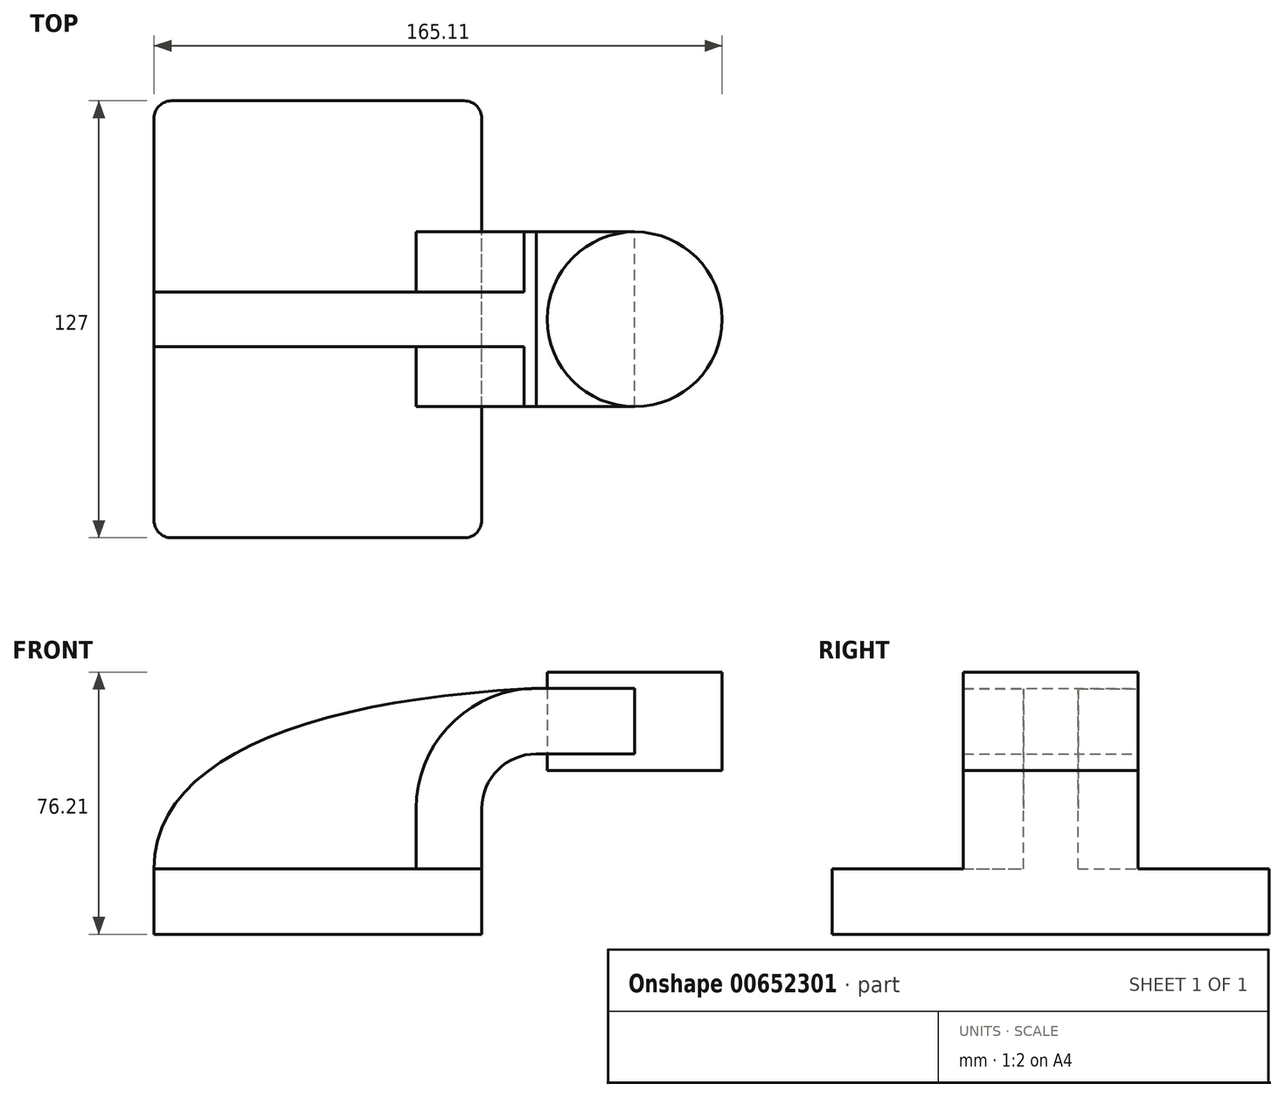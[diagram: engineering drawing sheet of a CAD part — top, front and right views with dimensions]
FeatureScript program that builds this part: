
annotation { "Feature Type Name" : "Feature", "Feature Type Description" : "" }
export const myFeature = defineFeature(function(context is Context, id is Id, definition is map)
    precondition{}
    {
        {
            var Q0;
            Q0=qCreatedBy(makeId("Front.planeOp"),FACE);
            var sketch = newSketch(context, id + "F0", { "sketchPlane" : qUnion([Q0])});
            skLineSegment(sketch, "E0.bottom", {"start": v(47.63, -9.52) * mm, "end": v(-47.62, -9.52) * mm});
            skLineSegment(sketch, "E0.top", {"start": v(47.62, 9.53) * mm, "end": v(-47.62, 9.53) * mm});
            skLineSegment(sketch, "E0.left", {"start": v(47.63, -9.52) * mm, "end": v(47.62, 9.53) * mm});
            skLineSegment(sketch, "E0.right", {"start": v(-47.62, -9.52) * mm, "end": v(-47.62, 9.53) * mm});
            skPoint(sketch, "E0.middle", {"position": v(0, 0) * mm});
            skLineSegment(sketch, "E1.bottom", {"start": v(66.67, 66.68) * mm, "end": v(117.47, 66.68) * mm});
            skLineSegment(sketch, "E1.top", {"start": v(66.67, 38.1) * mm, "end": v(117.47, 38.1) * mm});
            skLineSegment(sketch, "E1.left", {"start": v(66.67, 66.68) * mm, "end": v(66.67, 38.1) * mm});
            skLineSegment(sketch, "E1.right", {"start": v(117.47, 66.68) * mm, "end": v(117.47, 38.1) * mm});
            skPoint(sketch, "E1.middle", {"position": v(92.07, 52.39) * mm});
            skLineSegment(sketch, "E2", {"start": v(47.62, 9.53) * mm, "end": v(47.62, 27) * mm});
            skArc(sketch, "E3", {"start": v(47.62, 27) * mm, "mid": v(52.27, 38.23) * mm, "end": v(63.5, 42.88) * mm});
            skLineSegment(sketch, "E4", {"start": v(63.5, 42.88) * mm, "end": v(92.08, 42.88) * mm});
            skLineSegment(sketch, "E5.0", {"start": v(63.5, 61.93) * mm, "end": v(92.08, 61.93) * mm});
            skArc(sketch, "E5.1", {"start": v(28.58, 27) * mm, "mid": v(38.8, 51.7) * mm, "end": v(63.5, 61.93) * mm});
            skLineSegment(sketch, "E5.2", {"start": v(28.58, 9.53) * mm, "end": v(28.58, 27) * mm});
            skFitSpline(sketch, "E6", {"points": [v(-47.62, 9.53) * mm, v(63.5, 61.93) * mm], "startDerivative": vector(0.22, 99.5) * mm, "endDerivative": vector(190.5, 8.86) * mm});
            skLineSegment(sketch, "E7", {"start": v(92.07, 38.1) * mm, "end": v(92.07, 66.68) * mm});
            skSolve(sketch);
        }
        {
            var Q0;
            Q0=makeQuery(id+"F0.imprint","IMPRINT",FACE,{"disambiguationData":[TD([[makeQuery(id+"F0.imprint","IMPRINT",EDGE,{"derivedFrom":sQuery(id+"F0.wireOp",EDGE,"E0.bottom")}),-1.0]])]});
            extrude(context, id + "F1", {"entities" : qUnion([Q0]), "endBound" : BoundingType.SYMMETRIC, "depth" : 127 * mm, "offsetDistance" : 25.4 * mm});
        }
        {
            var Q0;
            {var subQ1=sQuery(id+"F0.wireOp",EDGE,"E2");Q0=makeQuery(id+"F0.imprint","IMPRINT",FACE,{"disambiguationData":[TD([[makeQuery(id+"F0.imprint","IMPRINT",EDGE,{"derivedFrom":subQ1}),1.0]])]});}
            var Q1;
            {var subQ0=sQuery(id+"F0.wireOp",EDGE,"E5.0");var subQ1=sQuery(id+"F0.wireOp",EDGE,"E1.left");var subQ2=makeQuery(id+"F0.imprint","INTERSECT",VERTEX,{"derivedFrom":[subQ1,subQ0]});Q1=makeQuery(id+"F0.imprint","IMPRINT",FACE,{"disambiguationData":[TD([[makeQuery(id+"F0.imprint","IMPRINT",EDGE,{"disambiguationData":[TD([[subQ2,-1.0]])],"derivedFrom":subQ1}),1.0]])]});}
            extrude(context, id + "F2", {"entities" : qUnion([Q0, Q1]), "operationType" : NewBodyOperationType.ADD, "endBound" : BoundingType.SYMMETRIC, "depth" : 50.8 * mm, "offsetDistance" : 25.4 * mm});
        }
        {
            var Q0;
            {var subQ3=sQuery(id+"F0.wireOp",EDGE,"E5.2");Q0=makeQuery(id+"F0.imprint","IMPRINT",FACE,{"disambiguationData":[TD([[makeQuery(id+"F0.imprint","IMPRINT",EDGE,{"derivedFrom":subQ3}),1.0]])]});}
            extrude(context, id + "F3", {"entities" : qUnion([Q0]), "operationType" : NewBodyOperationType.ADD, "endBound" : BoundingType.SYMMETRIC, "depth" : 15.88 * mm, "offsetDistance" : 25.4 * mm});
        }
        {
            var Q0;
            {var subQ4=sQuery(id+"F0.wireOp",EDGE,"E1.right");Q0=makeQuery(id+"F0.imprint","IMPRINT",FACE,{"disambiguationData":[TD([[makeQuery(id+"F0.imprint","IMPRINT",EDGE,{"derivedFrom":subQ4}),-1.0]])]});}
            var Q1;
            Q1=sQuery(id+"F0.wireOp",EDGE,"E7");
            revolve(context, id + "F4", {"entities" : qUnion([Q0]), "axis" : qUnion([Q1]), "revolveType" : RevolveType.FULL});
        }
        {
            var Q0;
            Q0=makeQuery(id+"F1.opExtrude","CAP_EDGE",EDGE,{"disambiguationData":[OSD([sQuery(id+"F0.wireOp",EDGE,"E0.right")])],"isStart":false});
            var Q1;
            Q1=makeQuery(id+"F1.opExtrude","CAP_EDGE",EDGE,{"disambiguationData":[OSD([sQuery(id+"F0.wireOp",EDGE,"E0.left")])],"isStart":false});
            var Q2;
            Q2=makeQuery(id+"F1.opExtrude","CAP_EDGE",EDGE,{"disambiguationData":[OSD([sQuery(id+"F0.wireOp",EDGE,"E0.left")])],"isStart":true});
            var Q3;
            Q3=makeQuery(id+"F1.opExtrude","CAP_EDGE",EDGE,{"disambiguationData":[OSD([sQuery(id+"F0.wireOp",EDGE,"E0.right")])],"isStart":true});
            fillet(context, id + "F5", {"entities" : qUnion([Q0, Q1, Q2, Q3]), "radius" : 5.08 * mm, "tangentPropagation" : true, "allowEdgeOverflow" : false});
        }
    });
